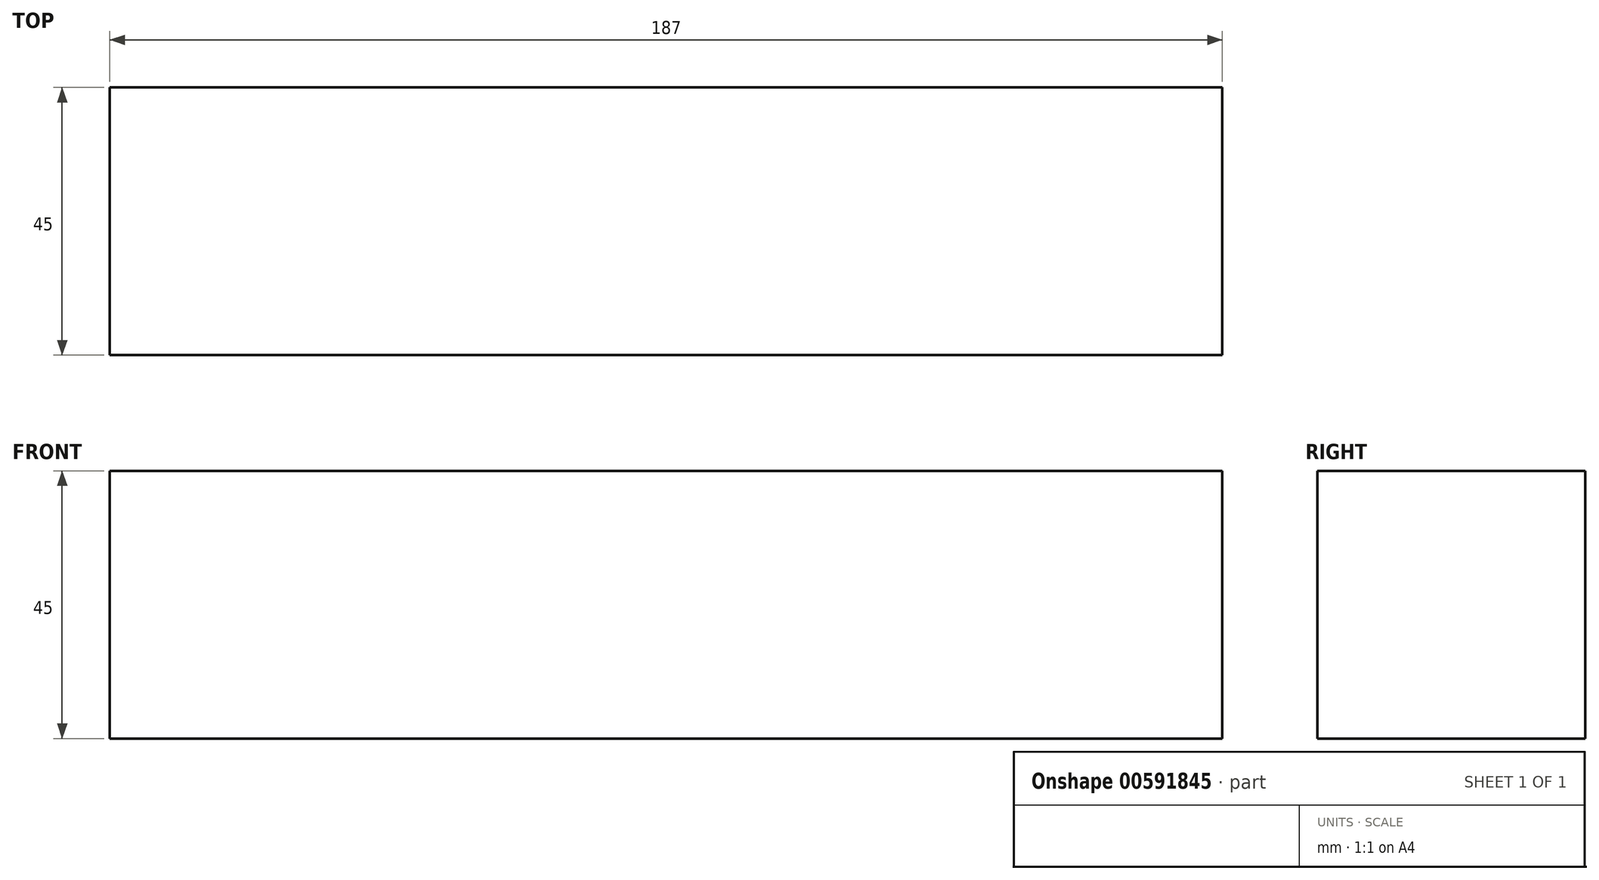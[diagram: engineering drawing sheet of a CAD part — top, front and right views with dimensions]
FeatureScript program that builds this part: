
annotation { "Feature Type Name" : "Feature", "Feature Type Description" : "" }
export const myFeature = defineFeature(function(context is Context, id is Id, definition is map)
    precondition{}
    {
        {
            var Q0;
            Q0=qCreatedBy(makeId("Right.planeOp"),FACE);
            var sketch = newSketch(context, id + "F0", { "sketchPlane" : qUnion([Q0])});
            skLineSegment(sketch, "E0.bottom", {"start": v(0, 0) * mm, "end": v(45, 0) * mm});
            skLineSegment(sketch, "E0.top", {"start": v(0, 45) * mm, "end": v(45, 45) * mm});
            skLineSegment(sketch, "E0.left", {"start": v(0, 0) * mm, "end": v(0, 45) * mm});
            skLineSegment(sketch, "E0.right", {"start": v(45, 0) * mm, "end": v(45, 45) * mm});
            skSolve(sketch);
        }
        {
            var Q0;
            Q0=makeQuery(id+"F0.imprint","IMPRINT",FACE,{"disambiguationData":[TD([[makeQuery(id+"F0.imprint","IMPRINT",EDGE,{"derivedFrom":sQuery(id+"F0.wireOp",EDGE,"E0.bottom")}),1.0]])]});
            extrude(context, id + "F1", {"entities" : qUnion([Q0]), "depth" : 187 * mm, "offsetDistance" : 25 * mm});
        }
    });
